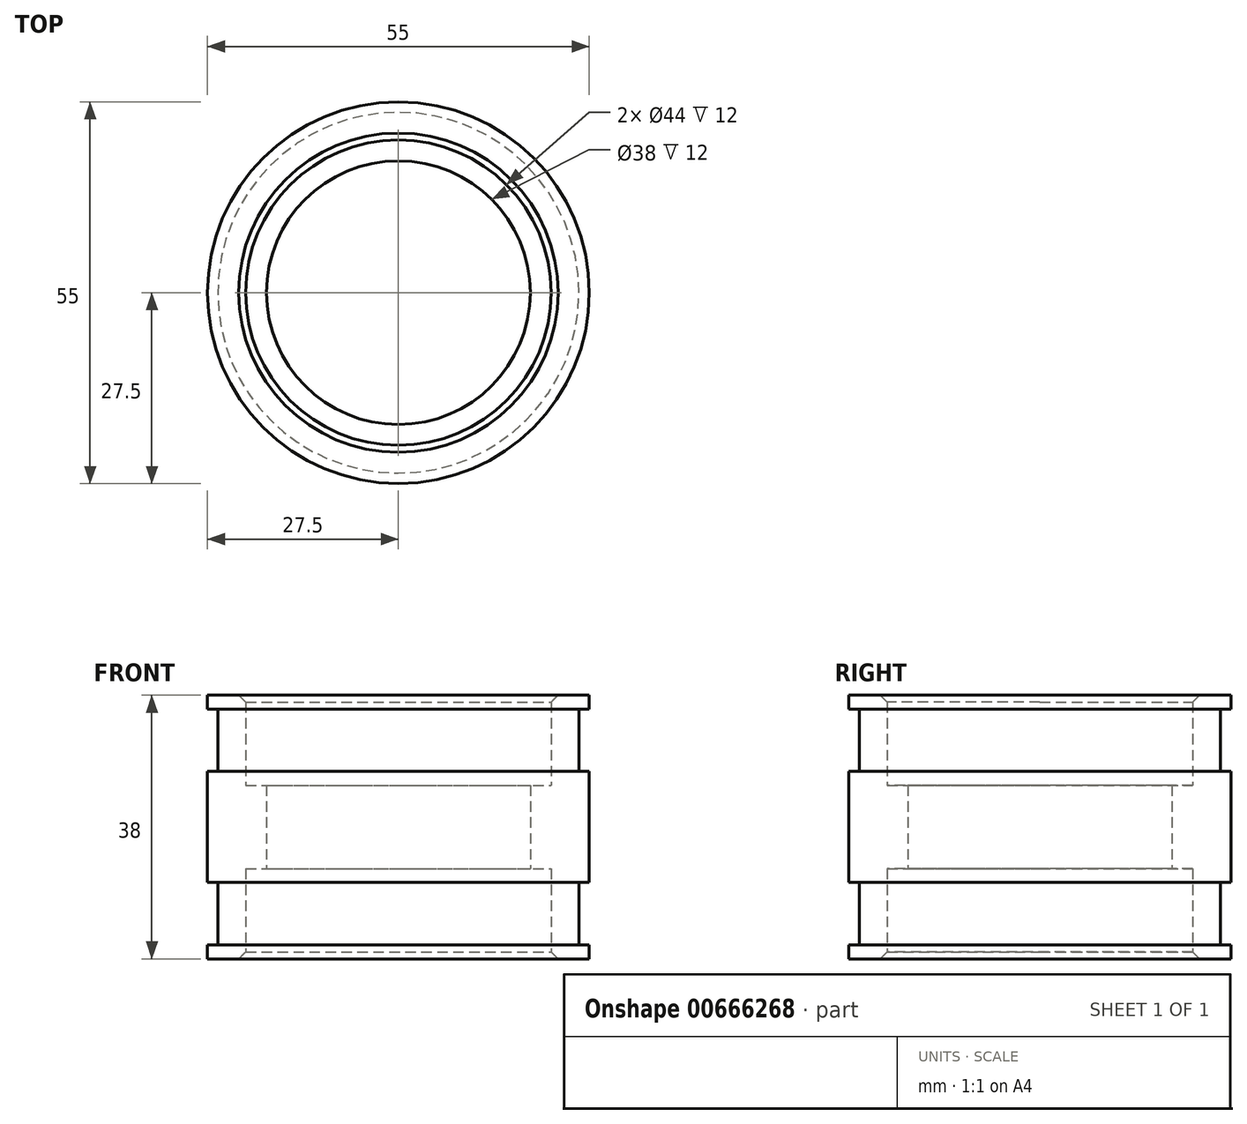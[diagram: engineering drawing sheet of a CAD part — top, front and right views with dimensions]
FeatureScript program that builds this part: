
annotation { "Feature Type Name" : "Feature", "Feature Type Description" : "" }
export const myFeature = defineFeature(function(context is Context, id is Id, definition is map)
    precondition{}
    {
        {
            var Q0;
            Q0=qCreatedBy(makeId("Front.planeOp"),FACE);
            var sketch = newSketch(context, id + "F0", { "sketchPlane" : qUnion([Q0])});
            skLineSegment(sketch, "E0", {"start": v(0, 0) * mm, "end": v(0, 96.12) * mm, "construction": true});
            skLineSegment(sketch, "E1", {"start": v(-22, 0) * mm, "end": v(-27.5, 0) * mm});
            skLineSegment(sketch, "E2", {"start": v(-27.5, 0) * mm, "end": v(-27.5, 2) * mm});
            skLineSegment(sketch, "E3", {"start": v(-27.5, 2) * mm, "end": v(-26, 2) * mm});
            skLineSegment(sketch, "E4", {"start": v(-26, 2) * mm, "end": v(-26, 11) * mm});
            skLineSegment(sketch, "E5", {"start": v(-26, 11) * mm, "end": v(-27.5, 11) * mm});
            skLineSegment(sketch, "E6", {"start": v(-27.5, 11) * mm, "end": v(-27.5, 27) * mm});
            skLineSegment(sketch, "E7", {"start": v(-27.5, 27) * mm, "end": v(-26, 27) * mm});
            skLineSegment(sketch, "E8", {"start": v(-26, 27) * mm, "end": v(-26, 36) * mm});
            skLineSegment(sketch, "E9", {"start": v(-26, 36) * mm, "end": v(-27.5, 36) * mm});
            skLineSegment(sketch, "E10", {"start": v(-27.5, 36) * mm, "end": v(-27.5, 38) * mm});
            skLineSegment(sketch, "E11", {"start": v(-27.5, 38) * mm, "end": v(-22, 38) * mm});
            skLineSegment(sketch, "E12", {"start": v(-22, 38) * mm, "end": v(-22, 0) * mm, "construction": true});
            skLineSegment(sketch, "E13", {"start": v(-22, 0) * mm, "end": v(-22, 13) * mm});
            skLineSegment(sketch, "E14", {"start": v(-22, 13) * mm, "end": v(-19, 13) * mm});
            skLineSegment(sketch, "E15", {"start": v(-19, 13) * mm, "end": v(-19, 25) * mm});
            skLineSegment(sketch, "E16", {"start": v(-19, 25) * mm, "end": v(-22, 25) * mm});
            skLineSegment(sketch, "E17", {"start": v(-22, 25) * mm, "end": v(-22, 38) * mm});
            skSolve(sketch);
        }
        {
            var Q0;
            Q0 = qSketchRegion(id + "F0", true);
            var Q1;
            Q1=sQuery(id+"F0.wireOp",EDGE,"E0");
            revolve(context, id + "F1", {"surfaceOperationType" : NewSurfaceOperationType.NEW, "entities" : qUnion([Q0]), "axis" : qUnion([Q1]), "revolveType" : RevolveType.FULL});
        }
        {
            var Q0;
            Q0=makeQuery(id+"F1.opRevolve","SWEPT_EDGE",EDGE,{"disambiguationData":[OSD([sQuery(id+"F0.wireOp",EDGE,"E11"),sQuery(id+"F0.wireOp",EDGE,"E17")])]});
            var Q1;
            Q1=makeQuery(id+"F1.opRevolve","SWEPT_EDGE",EDGE,{"disambiguationData":[OSD([sQuery(id+"F0.wireOp",EDGE,"E1"),sQuery(id+"F0.wireOp",EDGE,"E13")])]});
            chamfer(context, id + "F2", {"entities" : qUnion([Q0, Q1]), "width" : 1 * mm, "tangentPropagation" : true});
        }
    });
